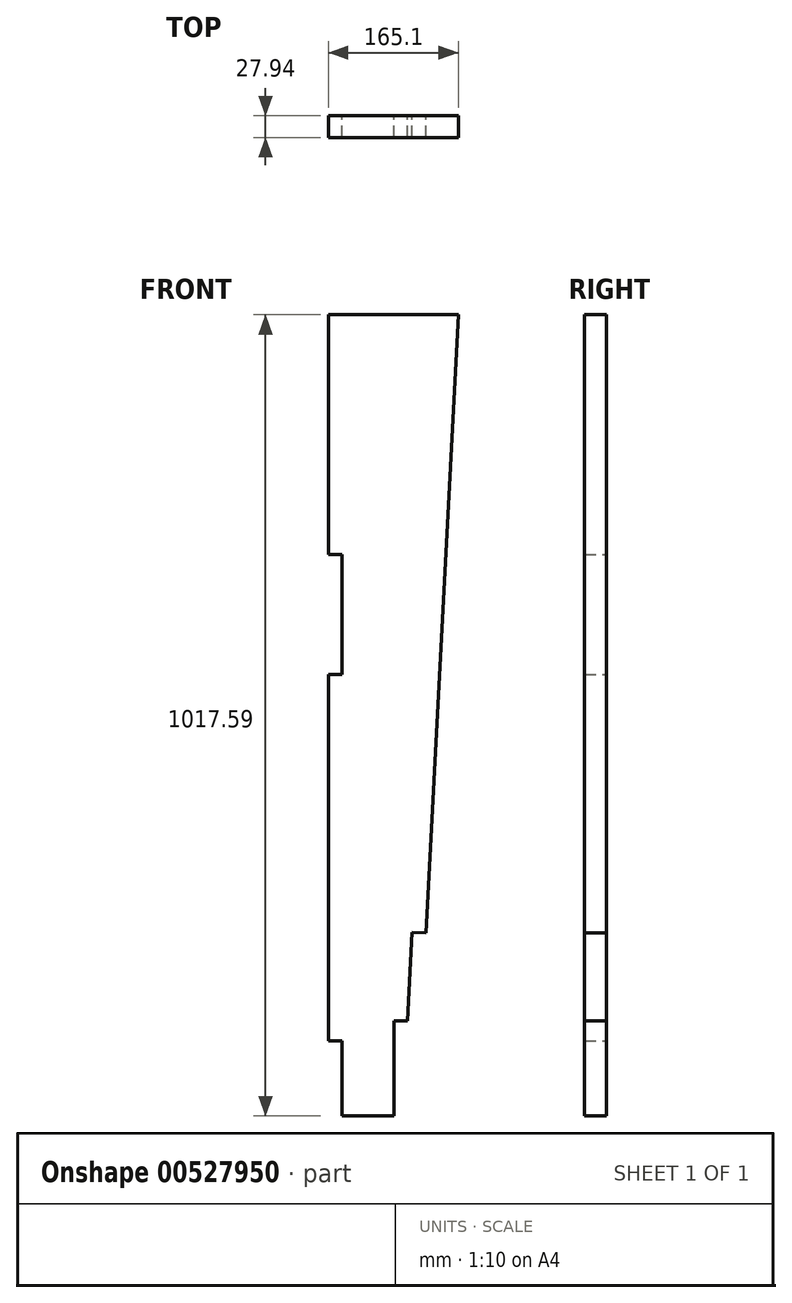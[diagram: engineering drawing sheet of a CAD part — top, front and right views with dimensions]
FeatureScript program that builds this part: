
annotation { "Feature Type Name" : "Feature", "Feature Type Description" : "" }
export const myFeature = defineFeature(function(context is Context, id is Id, definition is map)
    precondition{}
    {
        {
            var Q0;
            Q0=qCreatedBy(makeId("Front.planeOp"),FACE);
            var sketch = newSketch(context, id + "F0", { "sketchPlane" : qUnion([Q0])});
            skLineSegment(sketch, "E0", {"start": v(53.45, 674.07) * mm, "end": v(-111.65, 674.07) * mm});
            skLineSegment(sketch, "E1", {"start": v(-111.65, 674.07) * mm, "end": v(-111.65, 369.27) * mm});
            skLineSegment(sketch, "E2", {"start": v(-111.65, 369.27) * mm, "end": v(-94.18, 369.27) * mm});
            skLineSegment(sketch, "E3", {"start": v(-94.18, 369.27) * mm, "end": v(-94.18, 216.87) * mm});
            skLineSegment(sketch, "E4", {"start": v(-94.18, 216.87) * mm, "end": v(-111.65, 216.87) * mm});
            skLineSegment(sketch, "E5", {"start": v(-111.65, 216.87) * mm, "end": v(-111.65, -248.27) * mm});
            skLineSegment(sketch, "E6", {"start": v(-111.65, -248.27) * mm, "end": v(-94.18, -248.27) * mm});
            skLineSegment(sketch, "E7", {"start": v(-94.18, -248.27) * mm, "end": v(-94.18, -343.52) * mm});
            skLineSegment(sketch, "E8", {"start": v(-94.18, -343.52) * mm, "end": v(-28.58, -343.52) * mm});
            skLineSegment(sketch, "E9", {"start": v(-28.58, -343.52) * mm, "end": v(-28.58, -222.87) * mm});
            skLineSegment(sketch, "E10", {"start": v(-28.58, -222.87) * mm, "end": v(-11.11, -222.87) * mm});
            skLineSegment(sketch, "E11", {"start": v(-11.11, -222.87) * mm, "end": v(-5.14, -110.31) * mm});
            skLineSegment(sketch, "E12", {"start": v(53.45, 674.07) * mm, "end": v(12.3, -111.23) * mm});
            skLineSegment(sketch, "E13", {"start": v(-5.14, -110.31) * mm, "end": v(12.3, -111.23) * mm});
            skSolve(sketch);
        }
        {
            var Q0;
            Q0 = qSketchRegion(id + "F0", true);
            extrude(context, id + "F1", {"entities" : qUnion([Q0]), "depth" : 27.94 * mm, "offsetDistance" : 25.4 * mm});
        }
    });
